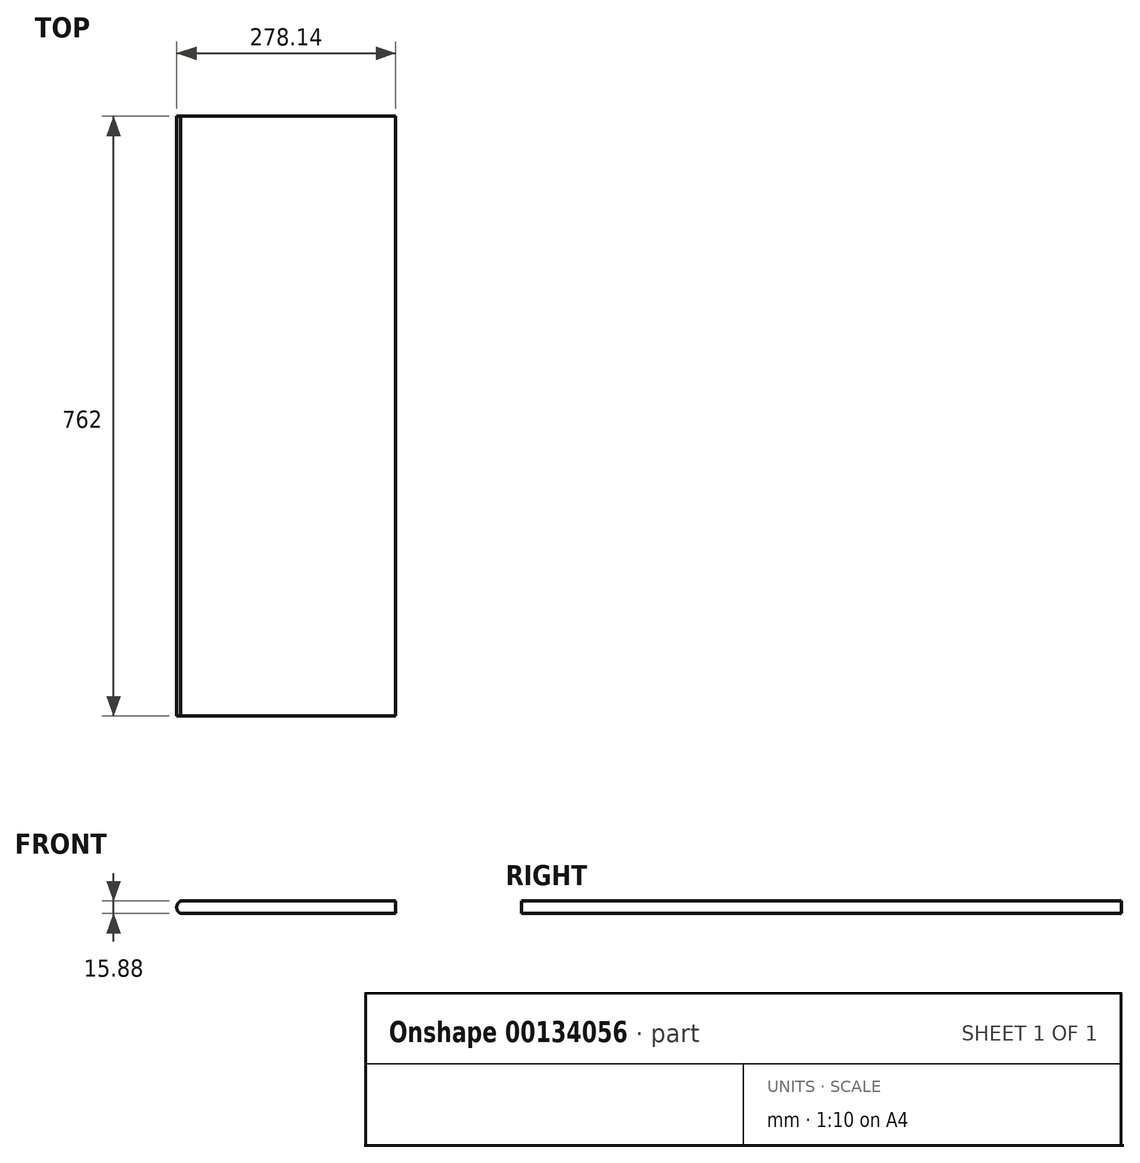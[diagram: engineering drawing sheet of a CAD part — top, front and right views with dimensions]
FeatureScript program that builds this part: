
annotation { "Feature Type Name" : "Feature", "Feature Type Description" : "" }
export const myFeature = defineFeature(function(context is Context, id is Id, definition is map)
    precondition{}
    {
        {
            var Q0;
            Q0=qCreatedBy(makeId("Front.planeOp"),FACE);
            var sketch = newSketch(context, id + "F0", { "sketchPlane" : qUnion([Q0])});
            skLineSegment(sketch, "E0.bottom", {"start": v(-136.52, -7.94) * mm, "end": v(136.53, -7.94) * mm});
            skLineSegment(sketch, "E0.top", {"start": v(-136.52, 7.94) * mm, "end": v(136.53, 7.94) * mm});
            skLineSegment(sketch, "E0.left", {"start": v(-136.52, -7.94) * mm, "end": v(-136.52, 7.94) * mm, "construction": true});
            skLineSegment(sketch, "E0.right", {"start": v(136.53, -7.94) * mm, "end": v(136.53, 7.94) * mm});
            skPoint(sketch, "E0.middle", {"position": v(0, 0) * mm});
            skArc(sketch, "E1", {"start": v(-136.52, 7.94) * mm, "mid": v(-141.6, 0) * mm, "end": v(-136.52, -7.94) * mm});
            skLineSegment(sketch, "E2", {"start": v(-132.86, 0) * mm, "end": v(-136.52, 0) * mm, "construction": true});
            skSolve(sketch);
        }
        {
            var Q0;
            Q0=makeQuery(id+"F0.imprint","IMPRINT",FACE,{"disambiguationData":[TD([[makeQuery(id+"F0.imprint","IMPRINT",EDGE,{"derivedFrom":sQuery(id+"F0.wireOp",EDGE,"E0.bottom")}),1.0]])]});
            extrude(context, id + "F1", {"entities" : qUnion([Q0]), "depth" : 762 * mm});
        }
    });
